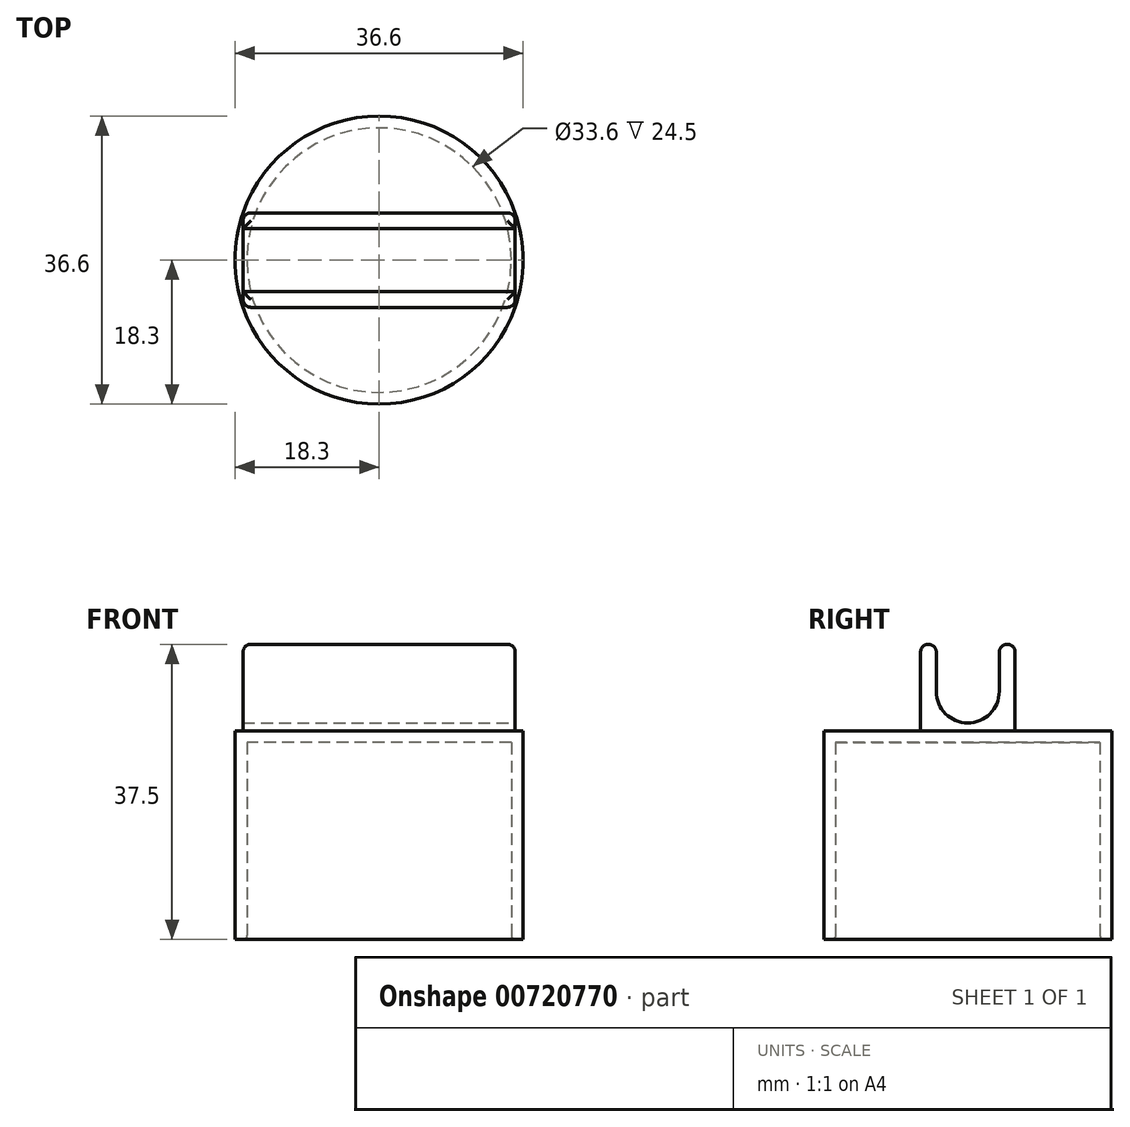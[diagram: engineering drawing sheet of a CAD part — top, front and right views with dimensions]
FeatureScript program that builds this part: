
annotation { "Feature Type Name" : "Feature", "Feature Type Description" : "" }
export const myFeature = defineFeature(function(context is Context, id is Id, definition is map)
    precondition{}
    {
        {
            var Q0;
            Q0=qCreatedBy(makeId("Top.planeOp"),FACE);
            var sketch = newSketch(context, id + "F0", { "sketchPlane" : qUnion([Q0])});
            skCircle(sketch, "E0", {"center": v(0, 0) * mm, "radius": 16.8 * mm});
            skCircle(sketch, "E1", {"center": v(0, 0) * mm, "radius": 18.3 * mm});
            skSolve(sketch);
        }
        {
            var Q0;
            Q0=makeQuery(id+"F0.imprint","IMPRINT",FACE,{"disambiguationData":[TD([[makeQuery(id+"F0.imprint","IMPRINT",EDGE,{"derivedFrom":sQuery(id+"F0.wireOp",EDGE,"E0")}),-1.0]])]});
            extrude(context, id + "F1", {"entities" : qUnion([Q0]), "depth" : 25 * mm, "offsetDistance" : 25 * mm});
        }
        {
            var Q0;
            Q0=makeQuery(id+"F1.opExtrude","CAP_FACE",FACE,{"disambiguationData":[OSD([sQuery(id+"F0.wireOp",EDGE,"E0"),sQuery(id+"F0.wireOp",EDGE,"E1")])],"isStart":false});
            var sketch = newSketch(context, id + "F2", { "sketchPlane" : qUnion([Q0])});
            skSolve(sketch);
        }
        {
            var Q0;
            Q0=makeQuery(id+"F2.imprint","IMPRINT",FACE,{"disambiguationData":[TD([[makeQuery(id+"F2.imprint","IMPRINT",EDGE,{"derivedFrom":makeQuery(id+"F1.opExtrude","CAP_EDGE",EDGE,{"disambiguationData":[OSD([sQuery(id+"F0.wireOp",EDGE,"E0")])],"isStart":false})}),-1.0]])]});
            var Q1;
            Q1=makeQuery(id+"F2.imprint","IMPRINT",FACE,{"disambiguationData":[TD([[makeQuery(id+"F2.imprint","IMPRINT",EDGE,{"derivedFrom":makeQuery(id+"F1.opExtrude","CAP_EDGE",EDGE,{"disambiguationData":[OSD([sQuery(id+"F0.wireOp",EDGE,"E0")])],"isStart":false})}),1.0]])]});
            extrude(context, id + "F3", {"entities" : qUnion([Q0, Q1]), "operationType" : NewBodyOperationType.ADD, "depth" : 1.5 * mm, "offsetDistance" : 25 * mm});
        }
        {
            var Q0;
            Q0=makeQuery(id+"F3.opExtrude","CAP_FACE",FACE,{"disambiguationData":[OSD([sQuery(id+"F0.wireOp",EDGE,"E1")])],"isStart":false});
            var sketch = newSketch(context, id + "F4", { "sketchPlane" : qUnion([Q0])});
            skPoint(sketch, "E2", {"position": v(0, 0) * mm});
            skLineSegment(sketch, "E3.bottom", {"start": v(17.29, -6) * mm, "end": v(-17.29, -6) * mm});
            skLineSegment(sketch, "E3.top", {"start": v(17.29, 6) * mm, "end": v(-17.29, 6) * mm});
            skLineSegment(sketch, "E3.left", {"start": v(17.29, -6) * mm, "end": v(17.29, 6) * mm});
            skLineSegment(sketch, "E3.right", {"start": v(-17.29, -6) * mm, "end": v(-17.29, 6) * mm});
            skSolve(sketch);
        }
        {
            var Q0;
            Q0=makeQuery(id+"F4.imprint","IMPRINT",FACE,{"disambiguationData":[TD([[makeQuery(id+"F4.imprint","IMPRINT",EDGE,{"derivedFrom":sQuery(id+"F4.wireOp",EDGE,"E3.bottom")}),-1.0]])]});
            extrude(context, id + "F5", {"entities" : qUnion([Q0]), "operationType" : NewBodyOperationType.ADD, "depth" : 5 * mm, "offsetDistance" : 25 * mm});
        }
        {
            var Q0;
            Q0=makeQuery(id+"F5.opExtrude","SWEPT_FACE",FACE,{"disambiguationData":[OSD([sQuery(id+"F4.wireOp",EDGE,"E3.left")])]});
            var sketch = newSketch(context, id + "F6", { "sketchPlane" : qUnion([Q0])});
            skCircle(sketch, "E4", {"center": v(0, 31.5) * mm, "radius": 4 * mm});
            skSolve(sketch);
        }
        {
            var Q0;
            {var subQ0=sQuery(id+"F6.wireOp",EDGE,"E4");var subQ1=makeQuery(id+"F5.opExtrude","CAP_EDGE",EDGE,{"disambiguationData":[OSD([sQuery(id+"F4.wireOp",EDGE,"E3.left")])],"isStart":false});var subQ2=makeQuery(id+"F6.imprint","INTERSECT",VERTEX,{"disambiguationData":[OD(0.0)],"derivedFrom":[subQ1,subQ0]});Q0=makeQuery(id+"F6.imprint","IMPRINT",FACE,{"disambiguationData":[TD([[makeQuery(id+"F6.imprint","IMPRINT",EDGE,{"disambiguationData":[TD([[subQ2,-1.0]])],"derivedFrom":subQ0}),1.0]])]});}
            extrude(context, id + "F7", {"entities" : qUnion([Q0]), "operationType" : NewBodyOperationType.REMOVE, "oppositeDirection" : true, "depth" : 36 * mm, "offsetDistance" : 25 * mm});
        }
        {
            var Q0;
            {var subQ0=sQuery(id+"F4.wireOp",EDGE,"E3.bottom");var subQ1=sQuery(id+"F4.wireOp",EDGE,"E3.right");var subQ2=sQuery(id+"F4.wireOp",EDGE,"E3.left");Q0=makeQuery(id+"F7.boolean.opBoolean","SPLIT",FACE,{"disambiguationData":[TD([makeQuery(id+"F5.opExtrude","SWEPT_FACE",FACE,{"disambiguationData":[OSD([subQ0])]})])],"derivedFrom":makeQuery(id+"F5.opExtrude","CAP_FACE",FACE,{"disambiguationData":[OSD([subQ0,sQuery(id+"F4.wireOp",EDGE,"E3.top"),subQ2,subQ1])],"isStart":false})});}
            var sketch = newSketch(context, id + "F8", { "sketchPlane" : qUnion([Q0])});
            skSolve(sketch);
        }
        {
            var Q0;
            {var subQ0=sQuery(id+"F4.wireOp",EDGE,"E3.bottom");Q0=makeQuery(id+"F8.imprint","IMPRINT",FACE,{"disambiguationData":[TD([[makeQuery(id+"F8.imprint","IMPRINT",EDGE,{"derivedFrom":makeQuery(id+"F5.opExtrude","CAP_EDGE",EDGE,{"disambiguationData":[OSD([subQ0])],"isStart":false})}),-1.0]])]});}
            var Q1;
            {var subQ0=sQuery(id+"F4.wireOp",EDGE,"E3.top");var subQ1=sQuery(id+"F4.wireOp",EDGE,"E3.left");var subQ2=sQuery(id+"F4.wireOp",EDGE,"E3.right");Q1=makeQuery(id+"F7.boolean.opBoolean","SPLIT",FACE,{"disambiguationData":[TD([makeQuery(id+"F5.opExtrude","SWEPT_FACE",FACE,{"disambiguationData":[OSD([subQ0])]})])],"derivedFrom":makeQuery(id+"F5.opExtrude","CAP_FACE",FACE,{"disambiguationData":[OSD([sQuery(id+"F4.wireOp",EDGE,"E3.bottom"),subQ0,subQ1,subQ2])],"isStart":false})});}
            extrude(context, id + "F9", {"entities" : qUnion([Q0, Q1]), "operationType" : NewBodyOperationType.ADD, "depth" : 6 * mm, "offsetDistance" : 25 * mm});
        }
        {
            var Q0;
            Q0=makeQuery(id+"F9.opExtrude","CAP_FACE",FACE,{"disambiguationData":[OSD([sQuery(id+"F4.wireOp",EDGE,"E3.bottom"),sQuery(id+"F4.wireOp",EDGE,"E3.top"),sQuery(id+"F4.wireOp",EDGE,"E3.left"),sQuery(id+"F4.wireOp",EDGE,"E3.right")])],"isStart":false});
            var Q1;
            {var subQ0=sQuery(id+"F4.wireOp",EDGE,"E3.left");var subQ1=sQuery(id+"F4.wireOp",EDGE,"E3.bottom");Q1=makeQuery(id+"F9.boolean.opBoolean","MERGE",EDGE,{"derivedFrom":[makeQuery(id+"F5.opExtrude","SWEPT_EDGE",EDGE,{"disambiguationData":[OSD([subQ1,subQ0])]}),makeQuery(id+"F9.opExtrude","SWEPT_EDGE",EDGE,{"disambiguationData":[OSD([subQ1,subQ0]),TDD([makeQuery(id+"F5.opExtrude","CAP_VERTEX",VERTEX,{"disambiguationData":[OSD([subQ1,subQ0])],"isStart":false})])]})]});}
            var Q2;
            {var subQ0=sQuery(id+"F4.wireOp",EDGE,"E3.right");var subQ1=sQuery(id+"F4.wireOp",EDGE,"E3.bottom");Q2=makeQuery(id+"F9.boolean.opBoolean","MERGE",EDGE,{"derivedFrom":[makeQuery(id+"F5.opExtrude","SWEPT_EDGE",EDGE,{"disambiguationData":[OSD([subQ1,subQ0])]}),makeQuery(id+"F9.opExtrude","SWEPT_EDGE",EDGE,{"disambiguationData":[OSD([subQ1,subQ0]),TDD([makeQuery(id+"F5.opExtrude","CAP_VERTEX",VERTEX,{"disambiguationData":[OSD([subQ1,subQ0])],"isStart":false})])]})]});}
            var Q3;
            {var subQ0=sQuery(id+"F4.wireOp",EDGE,"E3.right");var subQ1=sQuery(id+"F4.wireOp",EDGE,"E3.top");Q3=makeQuery(id+"F9.boolean.opBoolean","MERGE",EDGE,{"derivedFrom":[makeQuery(id+"F5.opExtrude","SWEPT_EDGE",EDGE,{"disambiguationData":[OSD([subQ1,subQ0])]}),makeQuery(id+"F9.opExtrude","SWEPT_EDGE",EDGE,{"disambiguationData":[OSD([subQ1,subQ0]),TDD([makeQuery(id+"F5.opExtrude","CAP_VERTEX",VERTEX,{"disambiguationData":[OSD([subQ1,subQ0])],"isStart":false})])]})]});}
            var Q4;
            Q4=makeQuery(id+"F9.opExtrude","CAP_FACE",FACE,{"disambiguationData":[OSD([sQuery(id+"F4.wireOp",EDGE,"E3.bottom"),sQuery(id+"F4.wireOp",EDGE,"E3.left"),sQuery(id+"F4.wireOp",EDGE,"E3.right"),sQuery(id+"F6.wireOp",EDGE,"E4")])],"isStart":false});
            fillet(context, id + "F10", {"entities" : qUnion([Q0, Q1, Q2, Q3, Q4]), "radius" : 1 * mm, "tangentPropagation" : true, "allowEdgeOverflow" : false});
        }
        {
            var Q0;
            {var subQ0=sQuery(id+"F4.wireOp",EDGE,"E3.left");var subQ1=sQuery(id+"F4.wireOp",EDGE,"E3.top");Q0=makeQuery(id+"F9.boolean.opBoolean","MERGE",EDGE,{"derivedFrom":[makeQuery(id+"F5.opExtrude","SWEPT_EDGE",EDGE,{"disambiguationData":[OSD([subQ1,subQ0])]}),makeQuery(id+"F9.opExtrude","SWEPT_EDGE",EDGE,{"disambiguationData":[OSD([subQ1,subQ0]),TDD([makeQuery(id+"F5.opExtrude","CAP_VERTEX",VERTEX,{"disambiguationData":[OSD([subQ1,subQ0])],"isStart":false})])]})]});}
            fillet(context, id + "F11", {"entities" : qUnion([Q0]), "radius" : 1 * mm, "tangentPropagation" : true, "allowEdgeOverflow" : false});
        }
        {
            var Q0;
            Q0=makeQuery(id+"F1.opExtrude","CAP_EDGE",EDGE,{"disambiguationData":[OSD([sQuery(id+"F0.wireOp",EDGE,"E0")])],"isStart":true});
            fillet(context, id + "F12", {"entities" : qUnion([Q0]), "radius" : .5 * mm, "tangentPropagation" : true, "allowEdgeOverflow" : false});
        }
    });
